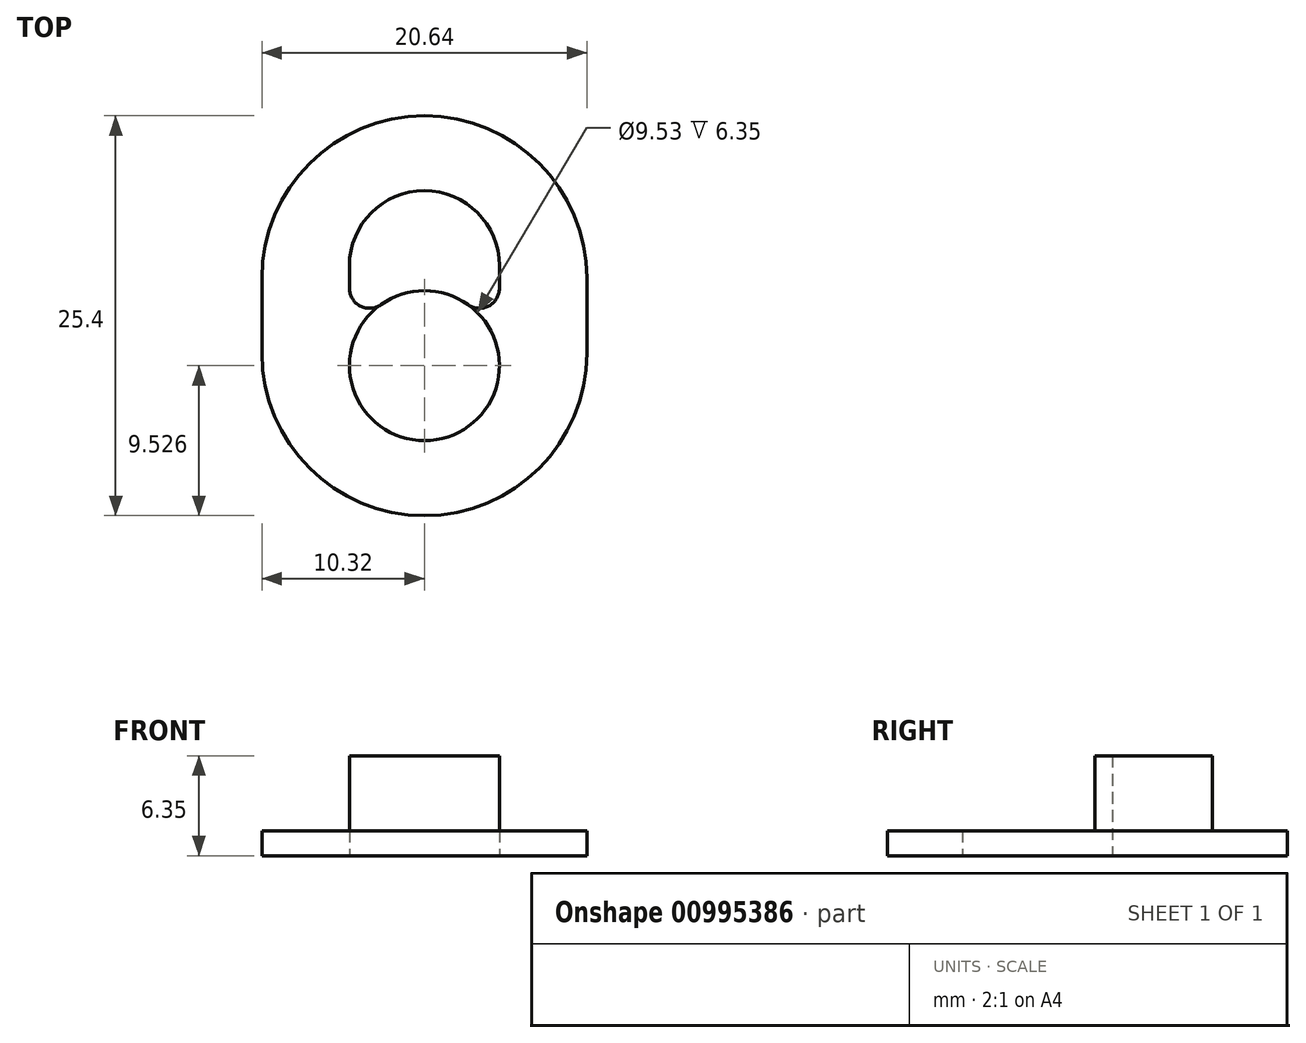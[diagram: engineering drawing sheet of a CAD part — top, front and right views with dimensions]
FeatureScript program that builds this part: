
annotation { "Feature Type Name" : "Feature", "Feature Type Description" : "" }
export const myFeature = defineFeature(function(context is Context, id is Id, definition is map)
    precondition{}
    {
        {
            var Q0;
            Q0=qCreatedBy(makeId("Top.planeOp"),FACE);
            var sketch = newSketch(context, id + "F0", { "sketchPlane" : qUnion([Q0])});
            skArc(sketch, "E0", {"start": v(-10.32, 0) * mm, "mid": v(0, -10.32) * mm, "end": v(10.32, 0) * mm});
            skArc(sketch, "E1", {"start": v(10.32, 4.76) * mm, "mid": v(0, 15.08) * mm, "end": v(-10.32, 4.76) * mm});
            skLineSegment(sketch, "E2", {"start": v(10.32, 4.76) * mm, "end": v(10.32, 0) * mm});
            skLineSegment(sketch, "E3.MirrorCS", {"start": v(-10.32, 4.76) * mm, "end": v(-10.32, 0) * mm});
            skCircle(sketch, "E4", {"center": v(0, -0.8) * mm, "radius": 4.76 * mm});
            skSolve(sketch);
        }
        {
            var Q0;
            Q0=makeQuery(id+"F0.imprint","IMPRINT",FACE,{"disambiguationData":[TD([[makeQuery(id+"F0.imprint","IMPRINT",EDGE,{"derivedFrom":sQuery(id+"F0.wireOp",EDGE,"E0")}),1.0]])]});
            extrude(context, id + "F1", {"entities" : qUnion([Q0]), "depth" : 1.59 * mm, "offsetDistance" : 25 * mm});
        }
        {
            var Q0;
            Q0=makeQuery(id+"F1.opExtrude","CAP_FACE",FACE,{"disambiguationData":[OSD([sQuery(id+"F0.wireOp",EDGE,"E0"),sQuery(id+"F0.wireOp",EDGE,"E1"),sQuery(id+"F0.wireOp",EDGE,"E2"),sQuery(id+"F0.wireOp",EDGE,"E3.MirrorCS"),sQuery(id+"F0.wireOp",EDGE,"E4")])],"isStart":false});
            var sketch = newSketch(context, id + "F2", { "sketchPlane" : qUnion([Q0])});
            skArc(sketch, "E5.0", {"start": v(4.76, -0.8) * mm, "mid": v(0, 3.97) * mm, "end": v(-4.76, -0.8) * mm});
            skArc(sketch, "E6", {"start": v(4.76, 5.56) * mm, "mid": v(0, 10.32) * mm, "end": v(-4.76, 5.56) * mm});
            skLineSegment(sketch, "E7", {"start": v(4.76, -0.8) * mm, "end": v(4.76, 5.56) * mm});
            skLineSegment(sketch, "E8.MirrorCS", {"start": v(-4.76, -0.8) * mm, "end": v(-4.76, 5.56) * mm});
            skSolve(sketch);
        }
        {
            var Q0;
            Q0 = qSketchRegion(id + "F2", true);
            extrude(context, id + "F3", {"entities" : qUnion([Q0]), "operationType" : NewBodyOperationType.ADD, "depth" : 4.76 * mm, "offsetDistance" : 25.4 * mm});
        }
        {
            var Q0;
            Q0=makeQuery(id+"F3.opExtrude","SWEPT_EDGE",EDGE,{"disambiguationData":[OSD([sQuery(id+"F0.wireOp",EDGE,"E4"),sQuery(id+"F2.wireOp",EDGE,"E5.0"),sQuery(id+"F2.wireOp",EDGE,"E7")])]});
            var Q1;
            Q1=makeQuery(id+"F3.opExtrude","SWEPT_EDGE",EDGE,{"disambiguationData":[OSD([sQuery(id+"F0.wireOp",EDGE,"E4"),sQuery(id+"F2.wireOp",EDGE,"E5.0"),sQuery(id+"F2.wireOp",EDGE,"E8.MirrorCS")])]});
            fillet(context, id + "F4", {"entities" : qUnion([Q0, Q1]), "radius" : 1.27 * mm, "tangentPropagation" : true, "allowEdgeOverflow" : false});
        }
    });
